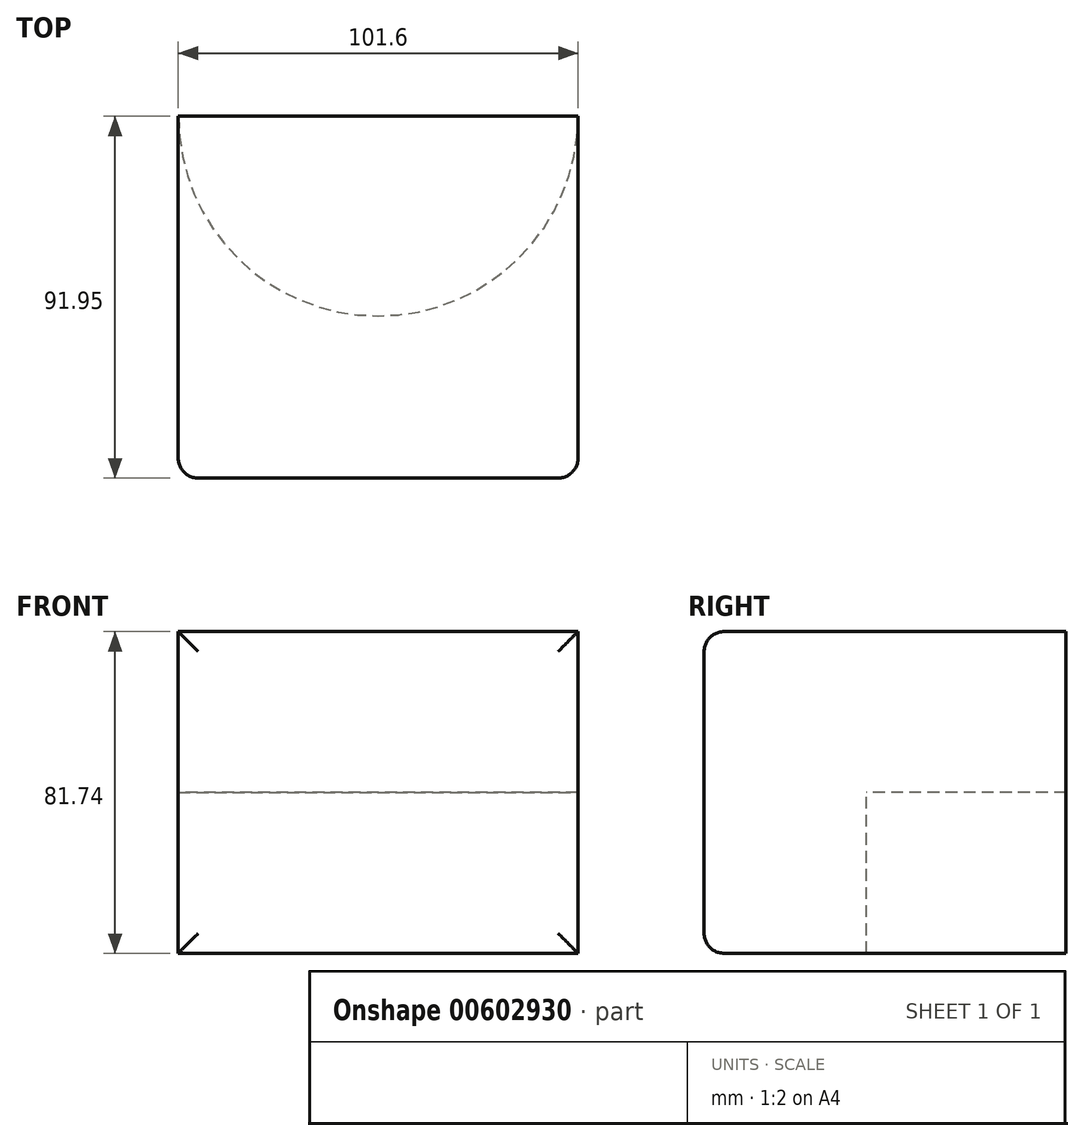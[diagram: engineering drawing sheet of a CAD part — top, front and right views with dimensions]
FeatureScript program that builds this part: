
annotation { "Feature Type Name" : "Feature", "Feature Type Description" : "" }
export const myFeature = defineFeature(function(context is Context, id is Id, definition is map)
    precondition{}
    {
        {
            var Q0;
            Q0=qCreatedBy(makeId("Front.planeOp"),FACE);
            var sketch = newSketch(context, id + "F0", { "sketchPlane" : qUnion([Q0])});
            skLineSegment(sketch, "E0.bottom", {"start": v(-50.8, -40.87) * mm, "end": v(50.8, -40.87) * mm});
            skLineSegment(sketch, "E0.top", {"start": v(-50.8, 40.87) * mm, "end": v(50.8, 40.87) * mm});
            skLineSegment(sketch, "E0.left", {"start": v(-50.8, -40.87) * mm, "end": v(-50.8, 40.87) * mm});
            skLineSegment(sketch, "E0.right", {"start": v(50.8, -40.87) * mm, "end": v(50.8, 40.87) * mm});
            skPoint(sketch, "E0.middle", {"position": v(0, 0) * mm});
            skSolve(sketch);
        }
        {
            var Q0;
            Q0 = qSketchRegion(id + "F0", true);
            extrude(context, id + "F1", {"entities" : qUnion([Q0]), "depth" : 91.95 * mm, "offsetDistance" : 25.4 * mm});
        }
        {
            var Q0;
            Q0=makeQuery(id+"F1.opExtrude","CAP_FACE",FACE,{"disambiguationData":[OSD([sQuery(id+"F0.wireOp",EDGE,"E0.bottom"),sQuery(id+"F0.wireOp",EDGE,"E0.top"),sQuery(id+"F0.wireOp",EDGE,"E0.left"),sQuery(id+"F0.wireOp",EDGE,"E0.right")])],"isStart":false});
            fillet(context, id + "F2", {"entities" : qUnion([Q0]), "radius" : 5.08 * mm, "tangentPropagation" : true, "allowEdgeOverflow" : false});
        }
        {
            var Q0;
            Q0=qCreatedBy(makeId("Top.planeOp"),FACE);
            var sketch = newSketch(context, id + "F3", { "sketchPlane" : qUnion([Q0])});
            skCircle(sketch, "E1", {"center": v(0, 0) * mm, "radius": 50.74 * mm});
            skSolve(sketch);
        }
        {
            var Q0;
            Q0 = qSketchRegion(id + "F3", true);
            extrude(context, id + "F4", {"entities" : qUnion([Q0]), "operationType" : NewBodyOperationType.REMOVE, "endBound" : BoundingType.THROUGH_ALL, "oppositeDirection" : true, "depth" : 105.16 * mm, "offsetDistance" : 25.4 * mm});
        }
    });
